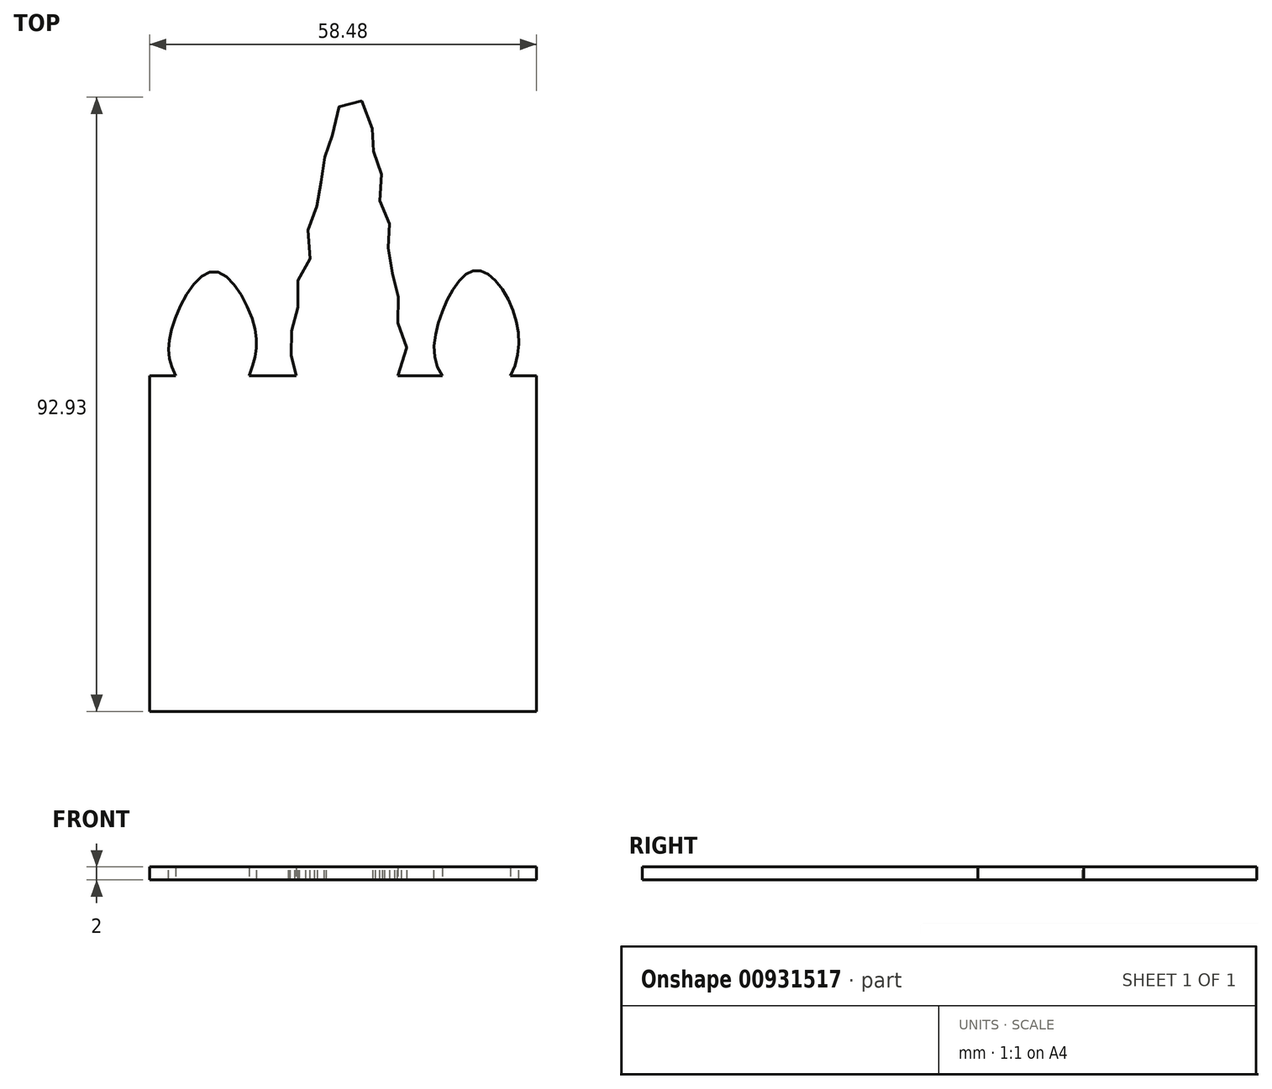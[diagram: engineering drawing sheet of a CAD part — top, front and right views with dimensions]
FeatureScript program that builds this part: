
annotation { "Feature Type Name" : "Feature", "Feature Type Description" : "" }
export const myFeature = defineFeature(function(context is Context, id is Id, definition is map)
    precondition{}
    {
        {
            var Q0;
            Q0=qCreatedBy(makeId("Top.planeOp"), FACE);
            var sketch = newSketch(context, id + "F0", { "sketchPlane" : qUnion([Q0])});
            skLineSegment(sketch, "E0", {"start": v(-25.4, 7.8) * mm, "end": v(-29.33, 7.8) * mm});
            skLineSegment(sketch, "E1", {"start": v(-29.33, 7.8) * mm, "end": v(-29.33, -42.97) * mm});
            skLineSegment(sketch, "E2", {"start": v(-29.33, -42.97) * mm, "end": v(29.15, -42.97) * mm});
            skLineSegment(sketch, "E3", {"start": v(29.15, -42.97) * mm, "end": v(29.15, 7.8) * mm});
            skLineSegment(sketch, "E4", {"start": v(29.15, 7.8) * mm, "end": v(25.22, 7.8) * mm});
            skFitSpline(sketch, "E5", {"points": [v(-25.4, 7.8) * mm, v(-25.88, 15.27) * mm, v(-19.6, 23.6) * mm, v(-13.52, 15.37) * mm, v(-14.29, 7.8) * mm], "startDerivative": vector(-15.62, 31.05) * mm, "endDerivative": vector(-13.04, -37.25) * mm});
            skLineSegment(sketch, "E6", {"start": v(-14.29, 7.8) * mm, "end": v(-7.18, 7.8) * mm});
            skFitSpline(sketch, "E7", {"points": [v(-7.18, 7.8) * mm, v(-8.26, 10.32) * mm, v(-7.38, 12.29) * mm, v(-8.04, 16.21) * mm, v(-6.71, 18.74) * mm, v(-6.85, 22.45) * mm, v(-5.13, 25.07) * mm, v(-5.66, 29.19) * mm, v(-3.98, 32.27) * mm, v(-4.33, 35.64) * mm, v(-2.64, 38.37) * mm, v(-2.93, 41.88) * mm, v(-1.68, 44.24) * mm, v(-0.82, 48.33) * mm, v(2.2, 49.84) * mm, v(3.93, 46.1) * mm, v(4.86, 43.56) * mm, v(4.49, 40.5) * mm, v(5.91, 37.74) * mm, v(5.5, 34.17) * mm, v(6.96, 31.3) * mm, v(6.26, 28.27) * mm, v(7.76, 25.18) * mm, v(7.03, 21.61) * mm, v(8.72, 18.88) * mm, v(8.16, 15.1) * mm, v(9.54, 11.96) * mm, v(8.2, 7.8) * mm], "startDerivative": vector(-82.76, 92.78) * mm, "endDerivative": vector(-55.17, -121.06) * mm});
            skLineSegment(sketch, "E8", {"start": v(8.2, 7.8) * mm, "end": v(14.96, 7.8) * mm});
            skFitSpline(sketch, "E9", {"points": [v(14.96, 7.8) * mm, v(14.89, 17.47) * mm, v(20.08, 23.79) * mm, v(25.55, 17.9) * mm, v(25.22, 7.8) * mm], "startDerivative": vector(-22.7, 29.99) * mm, "endDerivative": vector(-18.4, -34.85) * mm});
            skSolve(sketch);
        }
        {
            var Q0;
            Q0 = qSketchRegion(id + "F0", true);
            extrude(context, id + "F1", {"entities" : qUnion([Q0]), "depth" : 2 * mm, "offsetDistance" : 25 * mm});
        }
    });
